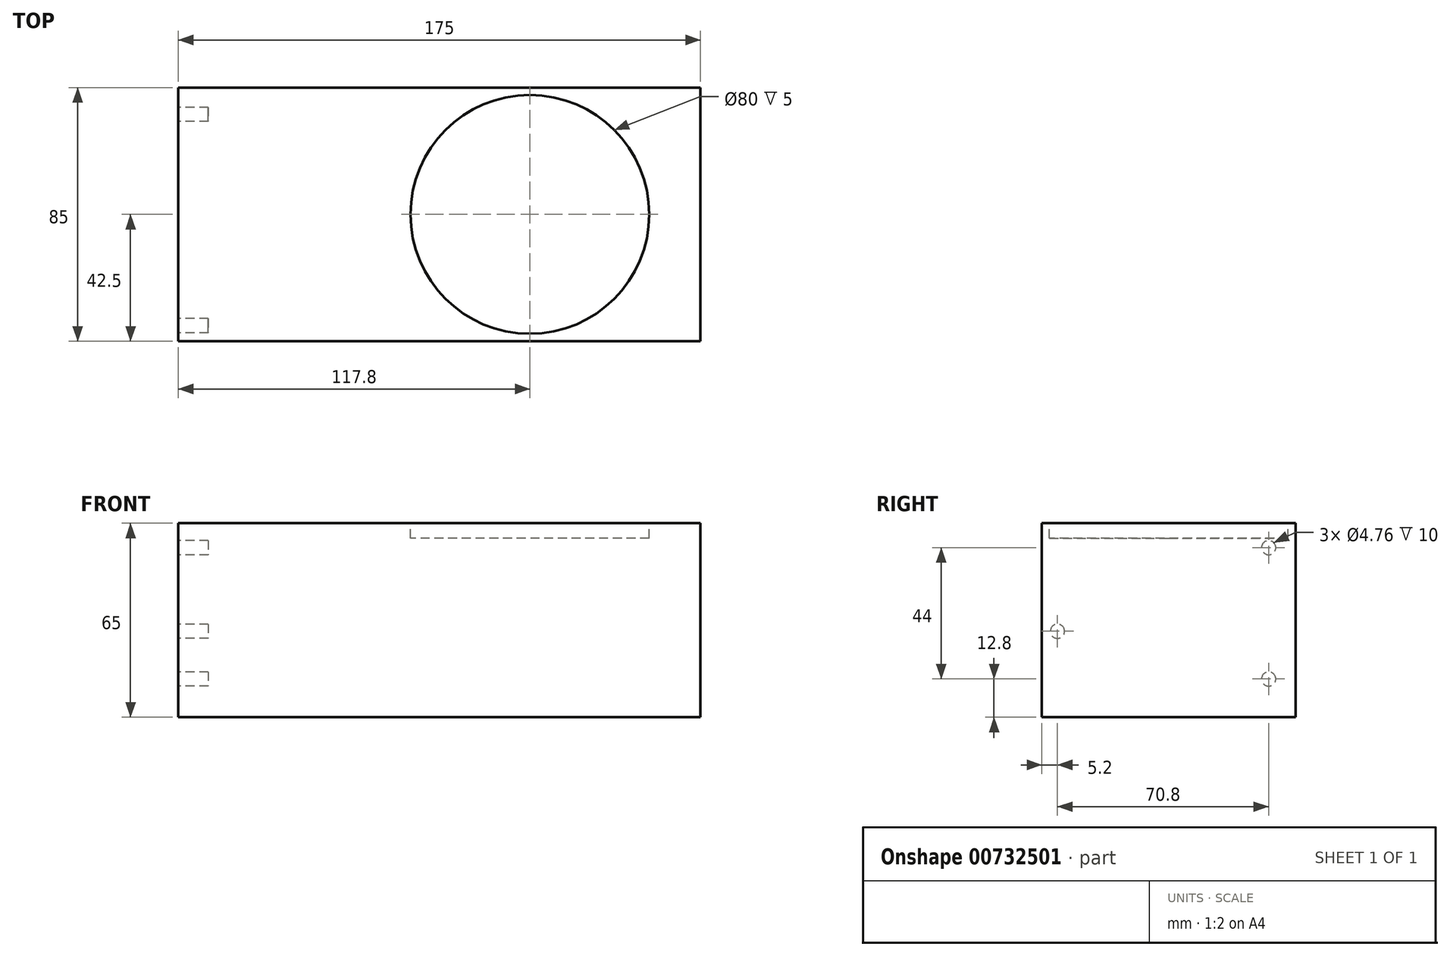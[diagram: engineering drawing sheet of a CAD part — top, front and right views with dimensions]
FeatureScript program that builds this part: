
annotation { "Feature Type Name" : "Feature", "Feature Type Description" : "" }
export const myFeature = defineFeature(function(context is Context, id is Id, definition is map)
    precondition{}
    {
        {
            var Q0;
            Q0=qCreatedBy(makeId("Top.planeOp"),FACE);
            var sketch = newSketch(context, id + "F0", { "sketchPlane" : qUnion([Q0])});
            skLineSegment(sketch, "E0.bottom", {"start": v(87.5, -42.5) * mm, "end": v(-87.5, -42.5) * mm});
            skLineSegment(sketch, "E0.top", {"start": v(87.5, 42.5) * mm, "end": v(-87.5, 42.5) * mm});
            skLineSegment(sketch, "E0.left", {"start": v(87.5, -42.5) * mm, "end": v(87.5, 42.5) * mm});
            skLineSegment(sketch, "E0.right", {"start": v(-87.5, -42.5) * mm, "end": v(-87.5, 42.5) * mm});
            skPoint(sketch, "E0.middle", {"position": v(0, 0) * mm});
            skSolve(sketch);
        }
        {
            var Q0;
            Q0 = qSketchRegion(id + "F0", true);
            extrude(context, id + "F1", {"entities" : qUnion([Q0]), "depth" : 65 * mm, "offsetDistance" : 25 * mm});
        }
        {
            var Q0;
            Q0=makeQuery(id+"F1.opExtrude","CAP_FACE",FACE,{"disambiguationData":[OSD([sQuery(id+"F0.wireOp",EDGE,"E0.bottom"),sQuery(id+"F0.wireOp",EDGE,"E0.top"),sQuery(id+"F0.wireOp",EDGE,"E0.left"),sQuery(id+"F0.wireOp",EDGE,"E0.right")])],"isStart":false});
            var sketch = newSketch(context, id + "F2", { "sketchPlane" : qUnion([Q0])});
            skLineSegment(sketch, "E1", {"start": v(-87.5, 0) * mm, "end": v(87.5, 0) * mm, "construction": true});
            skCircle(sketch, "E2", {"center": v(30.3, 0) * mm, "radius": 40 * mm});
            skSolve(sketch);
        }
        {
            var Q0;
            Q0 = qSketchRegion(id + "F2", true);
            extrude(context, id + "F3", {"entities" : qUnion([Q0]), "operationType" : NewBodyOperationType.REMOVE, "oppositeDirection" : true, "depth" : 5 * mm, "offsetDistance" : 25 * mm});
        }
        {
            var Q0;
            Q0=makeQuery(id+"F1.opExtrude","SWEPT_FACE",FACE,{"disambiguationData":[OSD([sQuery(id+"F0.wireOp",EDGE,"E0.right")])]});
            var sketch = newSketch(context, id + "F4", { "sketchPlane" : qUnion([Q0])});
            skCircle(sketch, "E3", {"center": v(-33.5, 12.8) * mm, "radius": 2.38 * mm});
            skCircle(sketch, "E4", {"center": v(-33.5, 56.8) * mm, "radius": 2.38 * mm});
            skCircle(sketch, "E5", {"center": v(37.3, 28.8) * mm, "radius": 2.38 * mm});
            skLineSegment(sketch, "E6", {"start": v(-33.5, 12.8) * mm, "end": v(-33.5, 56.8) * mm, "construction": true});
            skSolve(sketch);
        }
        {
            var Q0;
            Q0 = qSketchRegion(id + "F4", true);
            var Q1;
            Q1=sQuery(id+"F4.wireOp",EDGE,"E6");
            extrude(context, id + "F5", {"entities" : qUnion([Q0]), "operationType" : NewBodyOperationType.REMOVE, "surfaceEntities" : qUnion([Q1]), "oppositeDirection" : true, "depth" : 10 * mm, "offsetDistance" : 25 * mm});
        }
    });
